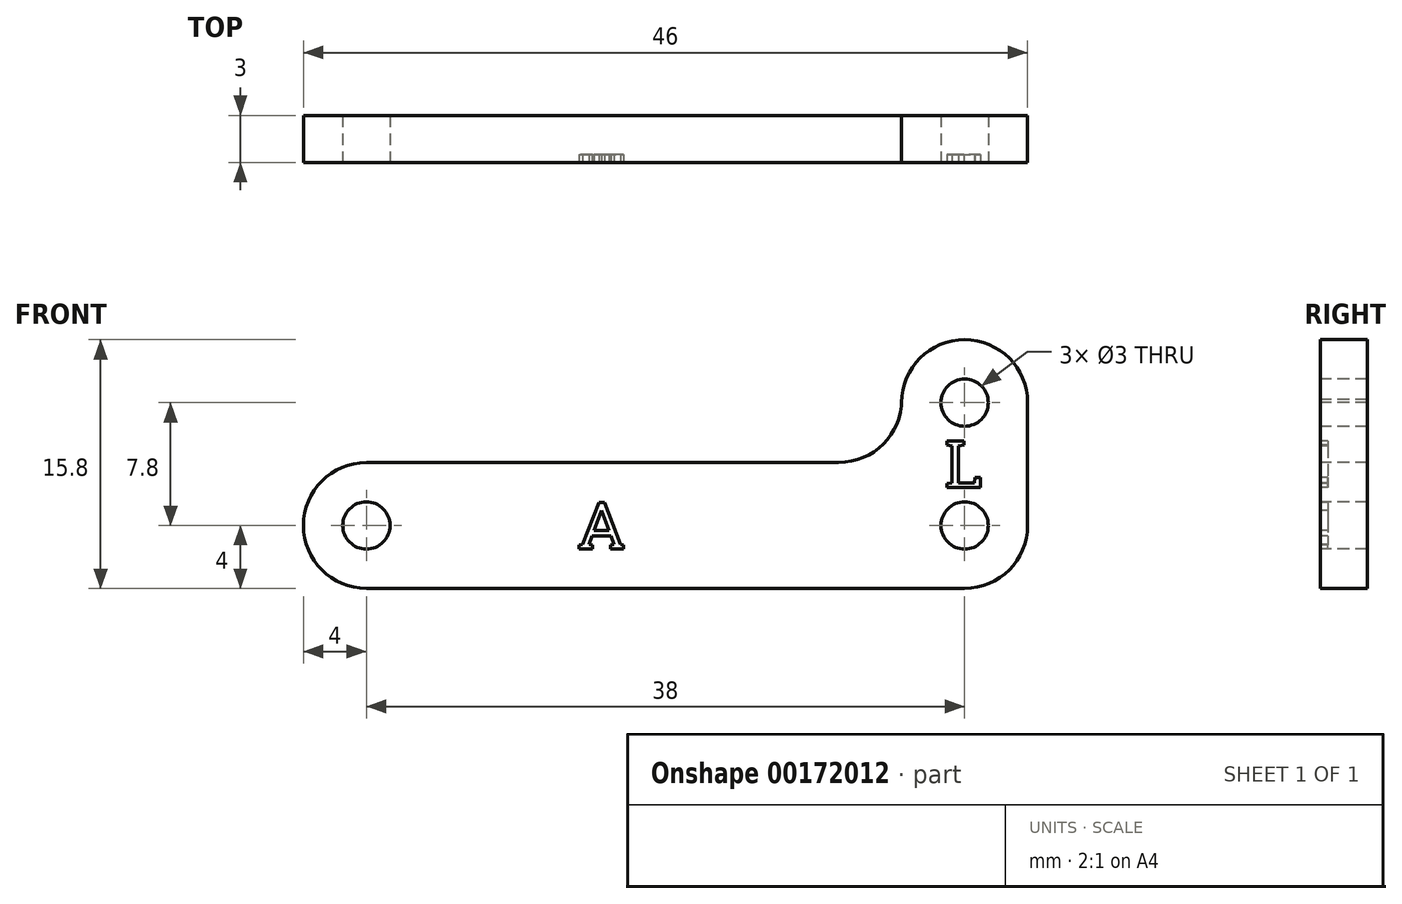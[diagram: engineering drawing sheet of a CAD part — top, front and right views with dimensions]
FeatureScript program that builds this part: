
annotation { "Feature Type Name" : "Feature", "Feature Type Description" : "" }
export const myFeature = defineFeature(function(context is Context, id is Id, definition is map)
    precondition{}
    {
        {
            assignVariable(context, id + "F0", {"name" : "Thickness", "anyValue" : 3});
        }
        {
            var Q0;
            Q0=qCreatedBy(makeId("Front.planeOp"),FACE);
            var sketch = newSketch(context, id + "F1", { "sketchPlane" : qUnion([Q0])});
            skCircle(sketch, "E0", {"center": v(-38, 0) * mm, "radius": 1.5 * mm});
            skCircle(sketch, "E1", {"center": v(0, 7.8) * mm, "radius": 1.5 * mm});
            skCircle(sketch, "E2", {"center": v(0, 0) * mm, "radius": 1.5 * mm});
            skArc(sketch, "E3", {"start": v(-38, 4) * mm, "mid": v(-42, 0) * mm, "end": v(-38, -4) * mm});
            skArc(sketch, "E4", {"start": v(4, 7.8) * mm, "mid": v(0, 11.8) * mm, "end": v(-4, 7.8) * mm});
            skArc(sketch, "E5", {"start": v(0, -4) * mm, "mid": v(2.83, -2.83) * mm, "end": v(4, 0) * mm});
            skArc(sketch, "E6", {"start": v(-8, 4) * mm, "mid": v(-5.17, 5.17) * mm, "end": v(-4, 8) * mm});
            skLineSegment(sketch, "E7", {"start": v(-38, 4) * mm, "end": v(-8, 4) * mm});
            skLineSegment(sketch, "E8", {"start": v(-4, 7.8) * mm, "end": v(-4, 8) * mm});
            skLineSegment(sketch, "E9", {"start": v(4, 7.8) * mm, "end": v(4, 0) * mm});
            skLineSegment(sketch, "E10", {"start": v(0, -4) * mm, "end": v(-38, -4) * mm});
            skSolve(sketch);
        }
        {
            var Q0;
            Q0=makeQuery(id+"F1.imprint","IMPRINT",FACE,{"disambiguationData":[TD([[makeQuery(id+"F1.imprint","IMPRINT",EDGE,{"derivedFrom":sQuery(id+"F1.wireOp",EDGE,"E0")}),-1.0]])]});
            extrude(context, id + "F2", {"entities" : qUnion([Q0]), "oppositeDirection" : true, "depth" : (getVariable(context, 'Thickness')) * mm});
        }
        {
            var Q0;
            Q0=qCreatedBy(makeId("Front.planeOp"),FACE);
            var sketch = newSketch(context, id + "F3", { "sketchPlane" : qUnion([Q0])});
            skText(sketch, "E11", { "text": "L", "fontName": "RobotoSlab-Regular.ttf"});
            skText(sketch, "E12", { "text": "A", "fontName": "RobotoSlab-Regular.ttf"});
            skLineSegment(sketch, "E13", {"start": v(-24.6, 0) * mm, "end": v(-21.4, 0) * mm, "construction": true});
            skLineSegment(sketch, "E14", {"start": v(4, 3.9) * mm, "end": v(1.27, 3.9) * mm, "construction": true});
            skLineSegment(sketch, "E15", {"start": v(-23, 4) * mm, "end": v(-23, 1.5) * mm, "construction": true});
            const initialGuessF3  = {"E11": [-0.00127, 0.0024, 1, 0, 0.003], "E12": [-0.0246, -0.0015, 1, 0, 0.003]};
            skSetInitialGuess(sketch, initialGuessF3);
            skSolve(sketch);
        }
        {
            assignVariable(context, id + "F4", {"name" : "DepthText", "anyValue" : .5});
        }
        {
            var Q0;
            Q0=qSketchRegion(id+"F3",true);
            extrude(context, id + "F5", {"entities" : qUnion([Q0]), "operationType" : NewBodyOperationType.REMOVE, "oppositeDirection" : true, "depth" : (getVariable(context, 'DepthText')) * mm});
        }
    });
